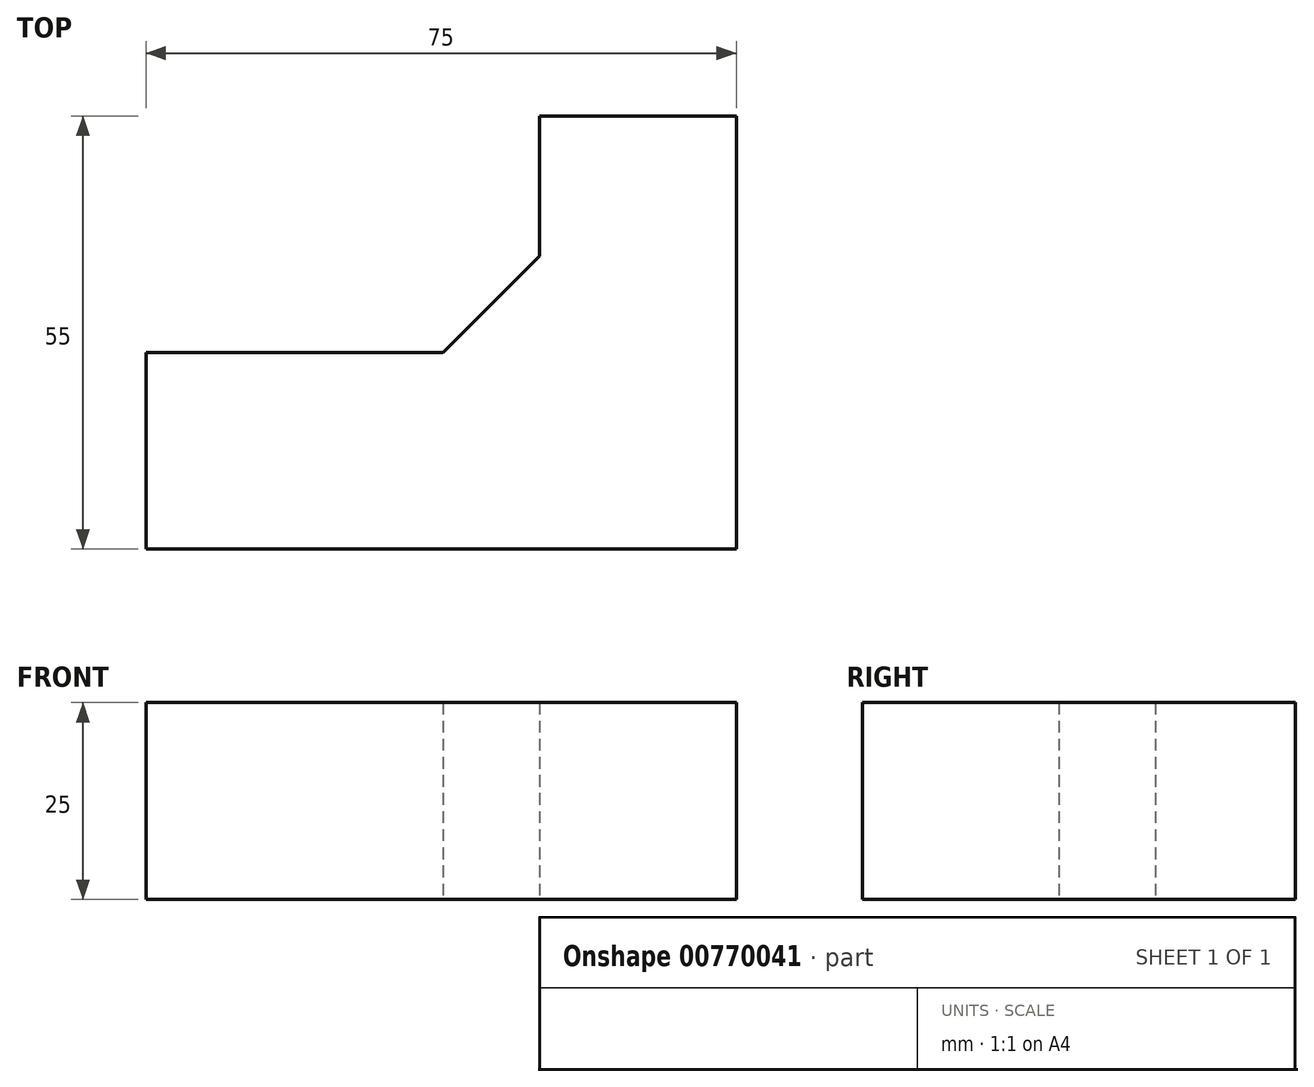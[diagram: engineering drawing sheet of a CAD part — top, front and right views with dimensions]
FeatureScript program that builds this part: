
annotation { "Feature Type Name" : "Feature", "Feature Type Description" : "" }
export const myFeature = defineFeature(function(context is Context, id is Id, definition is map)
    precondition{}
    {
        {
            var Q0;
            Q0=qCreatedBy(makeId("Top.planeOp"),FACE);
            var sketch = newSketch(context, id + "F0", { "sketchPlane" : qUnion([Q0])});
            skLineSegment(sketch, "E0", {"start": v(0, 0) * mm, "end": v(75, 0) * mm});
            skLineSegment(sketch, "E1", {"start": v(75, 0) * mm, "end": v(75, 55) * mm});
            skLineSegment(sketch, "E2", {"start": v(75, 55) * mm, "end": v(50, 55) * mm});
            skLineSegment(sketch, "E3", {"start": v(50, 55) * mm, "end": v(50, 37.25) * mm});
            skLineSegment(sketch, "E4", {"start": v(0, 0) * mm, "end": v(0, 25) * mm});
            skLineSegment(sketch, "E5", {"start": v(0, 25) * mm, "end": v(37.75, 25) * mm});
            skLineSegment(sketch, "E6", {"start": v(50, 37.25) * mm, "end": v(37.75, 25) * mm});
            skPoint(sketch, "E7.trimOffspring.end.orphan", {"position": v(50, 0) * mm});
            skSolve(sketch);
        }
        {
            var Q0;
            Q0=makeQuery(id+"F0.imprint","IMPRINT",FACE,{"disambiguationData":[TD([[makeQuery(id+"F0.imprint","IMPRINT",EDGE,{"derivedFrom":sQuery(id+"F0.wireOp",EDGE,"E0")}),1.0]])]});
            extrude(context, id + "F1", {"entities" : qUnion([Q0]), "depth" : 25 * mm, "offsetDistance" : 25 * mm});
        }
    });
